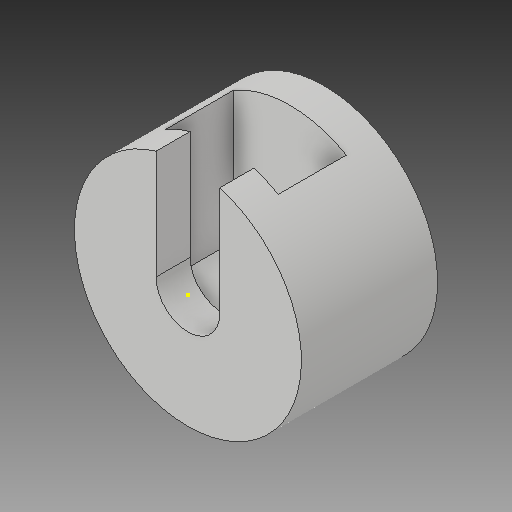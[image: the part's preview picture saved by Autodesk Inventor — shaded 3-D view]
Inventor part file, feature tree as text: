
AUTODESK INVENTOR PART (.ipt)
format: ipt  version: 2019 (Build 230136000, 136)  size: 133,632 bytes
history: native  units: mm
features: sketch x7, extrude x4, plane x1, hole x1, projected_geometry x1
ambient origin geometry x8: Origin, YZ Plane, XZ Plane, XY Plane, X Axis, Y Axis, Z Axis, Center Point
bodies: Solid1 (feature_tree)
feature tree (14):
  sketch  "Sketch1"  dims[d0=25.0mm d1=15.0mm d2=0.0mm]
  extrude  "Extrusion1"  Depth=15.0mm TaperAngle=0.0deg
  plane  "Work Plane1"
  extrude  "Extrusion2"  Depth=12.4mm
  extrude  "Extrusion3"  Depth=15.0mm TaperAngle=0.0deg
  hole  "Hole1"  [1 undecoded]
  sketch  "Sketch6"
  extrude  "Extrusion4"  [1 undecoded]
  sketch  "Sketch2"  dims[d3=7.5mm d4=12.4mm]
  sketch  "Sketch3"  dims[d5=7.5mm d6=0.0mm d7=15.0mm d8=0.0mm]
  sketch  "Sketch4"  dims[d9=7.0mm d10=6.0mm d11=5.0mm d12=3.0mm d13=90.0deg d14=7.5mm d15=0.0mm d16=15.0mm d17=0.0mm]
  sketch  "Sketch5"
  sketch  "Sketch7"
  projected_geometry  "Projected Loop1"
note: 2 required parameter values undecoded (feature->parameter linkage not recoverable at this tier; creation-order binding heuristic only, values carry confidence <= 0.55)
